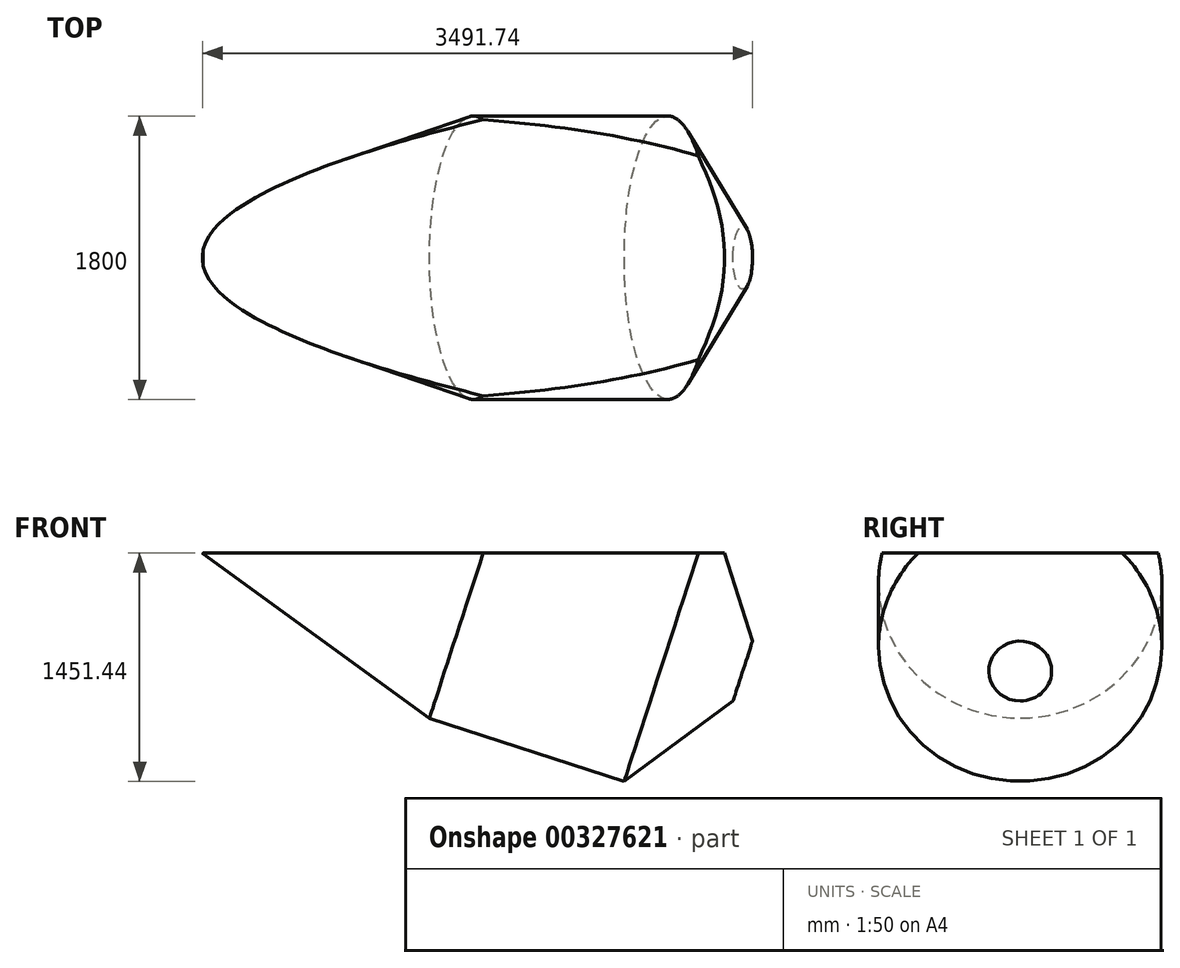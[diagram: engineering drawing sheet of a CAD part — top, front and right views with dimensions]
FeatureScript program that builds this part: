
annotation { "Feature Type Name" : "Feature", "Feature Type Description" : "" }
export const myFeature = defineFeature(function(context is Context, id is Id, definition is map)
    precondition{}
    {
        {
            var Q0;
            Q0=qCreatedBy(makeId("Front.planeOp"),FACE);
            var sketch = newSketch(context, id + "F0", { "sketchPlane" : qUnion([Q0])});
            skLineSegment(sketch, "E0", {"start": v(0, 0) * mm, "end": v(-3799.68, 1234.6) * mm, "construction": true});
            skLineSegment(sketch, "E1", {"start": v(0, 0) * mm, "end": v(-2814.72, 0) * mm, "construction": true});
            skLineSegment(sketch, "E2", {"start": v(-3213.62, 1412.18) * mm, "end": v(-1433.79, 1412.18) * mm});
            skLineSegment(sketch, "E3", {"start": v(-1433.79, 1412.18) * mm, "end": v(-197.41, 1010.46) * mm});
            skLineSegment(sketch, "E4", {"start": v(-197.41, 1010.46) * mm, "end": v(61.8, 190.21) * mm});
            skLineSegment(sketch, "E5", {"start": v(61.8, 190.21) * mm, "end": v(0, 0) * mm});
            skLineSegment(sketch, "E6", {"start": v(-3213.62, 1412.18) * mm, "end": v(-3321.78, 1079.31) * mm});
            skLineSegment(sketch, "E7", {"start": v(-3321.78, 1079.31) * mm, "end": v(0, 0) * mm});
            skSolve(sketch);
        }
        {
            var Q0;
            Q0 = qSketchRegion(id + "F0", true);
            var Q1;
            Q1=sQuery(id+"F0.wireOp",EDGE,"E0");
            revolve(context, id + "F1", {"entities" : qUnion([Q0]), "axis" : qUnion([Q1]), "revolveType" : RevolveType.FULL});
        }
        {
            var Q0;
            Q0=qCreatedBy(makeId("Front.planeOp"),FACE);
            var sketch = newSketch(context, id + "F2", { "sketchPlane" : qUnion([Q0])});
            skLineSegment(sketch, "E8", {"start": v(-3428.78, 750) * mm, "end": v(548.34, 750) * mm});
            skLineSegment(sketch, "E9", {"start": v(-3428.78, 750) * mm, "end": v(-3428.78, 1600) * mm});
            skLineSegment(sketch, "E10", {"start": v(-3428.78, 1600) * mm, "end": v(548.34, 1600) * mm});
            skLineSegment(sketch, "E11", {"start": v(548.34, 1600) * mm, "end": v(548.34, 750) * mm});
            skSolve(sketch);
        }
        {
            var Q0;
            Q0=makeQuery(id+"F2.imprint","IMPRINT",FACE,{"disambiguationData":[TD([[makeQuery(id+"F2.imprint","IMPRINT",EDGE,{"derivedFrom":sQuery(id+"F2.wireOp",EDGE,"E8")}),1.0]])]});
            extrude(context, id + "F3", {"entities" : qUnion([Q0]), "operationType" : NewBodyOperationType.REMOVE, "endBound" : BoundingType.SYMMETRIC, "oppositeDirection" : true, "depth" : 1800 * mm});
        }
    });
